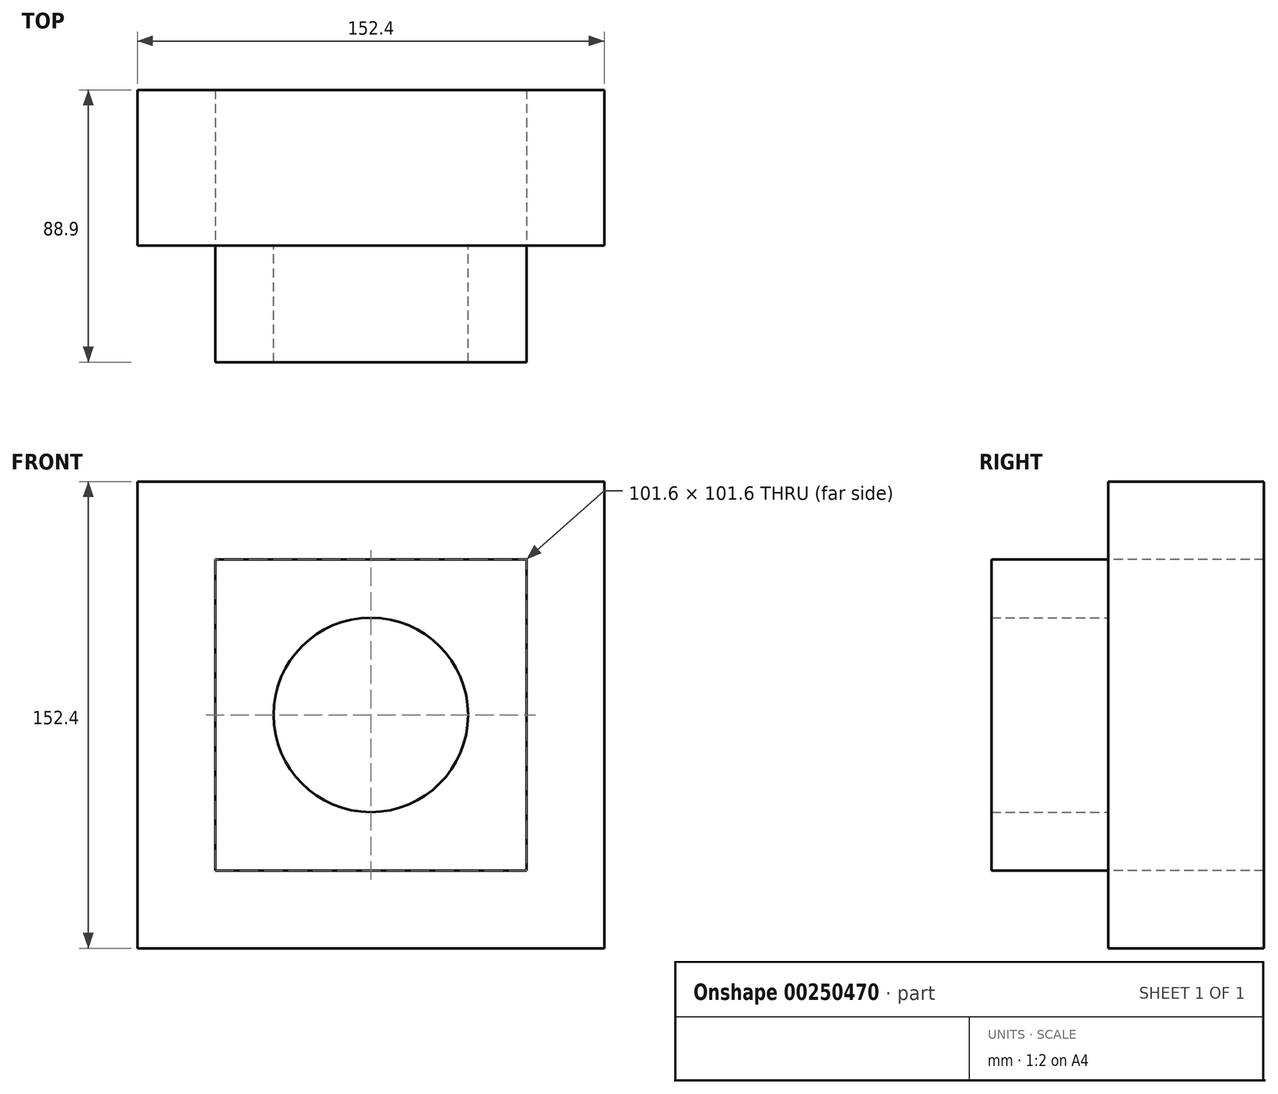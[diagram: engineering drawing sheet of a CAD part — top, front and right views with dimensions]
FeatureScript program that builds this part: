
annotation { "Feature Type Name" : "Feature", "Feature Type Description" : "" }
export const myFeature = defineFeature(function(context is Context, id is Id, definition is map)
    precondition{}
    {
        {
            var Q0;
            Q0=qCreatedBy(makeId("Front.planeOp"),FACE);
            var sketch = newSketch(context, id + "F0", { "sketchPlane" : qUnion([Q0])});
            skCircle(sketch, "E0", {"center": v(0, 0) * mm, "radius": 31.75 * mm});
            skLineSegment(sketch, "E1.bottom", {"start": v(50.8, 50.8) * mm, "end": v(-50.8, 50.8) * mm});
            skLineSegment(sketch, "E1.top", {"start": v(50.8, -50.8) * mm, "end": v(-50.8, -50.8) * mm});
            skLineSegment(sketch, "E1.left", {"start": v(50.8, 50.8) * mm, "end": v(50.8, -50.8) * mm});
            skLineSegment(sketch, "E1.right", {"start": v(-50.8, 50.8) * mm, "end": v(-50.8, -50.8) * mm});
            skLineSegment(sketch, "E2.bottom", {"start": v(76.2, 76.2) * mm, "end": v(-76.2, 76.2) * mm});
            skLineSegment(sketch, "E2.top", {"start": v(76.2, -76.2) * mm, "end": v(-76.2, -76.2) * mm});
            skLineSegment(sketch, "E2.left", {"start": v(76.2, 76.2) * mm, "end": v(76.2, -76.2) * mm});
            skLineSegment(sketch, "E2.right", {"start": v(-76.2, 76.2) * mm, "end": v(-76.2, -76.2) * mm});
            skSolve(sketch);
        }
        {
            var Q0;
            Q0=makeQuery(id+"F0.imprint","IMPRINT",FACE,{"disambiguationData":[TD([[makeQuery(id+"F0.imprint","IMPRINT",EDGE,{"derivedFrom":sQuery(id+"F0.wireOp",EDGE,"E0")}),-1.0]])]});
            extrude(context, id + "F1", {"entities" : qUnion([Q0]), "depth" : 38.1 * mm});
        }
        {
            var Q0;
            Q0 = qSketchRegion(id + "F0", true);
            extrude(context, id + "F2", {"entities" : qUnion([Q0]), "operationType" : NewBodyOperationType.ADD, "oppositeDirection" : true, "depth" : 50.8 * mm});
        }
    });
